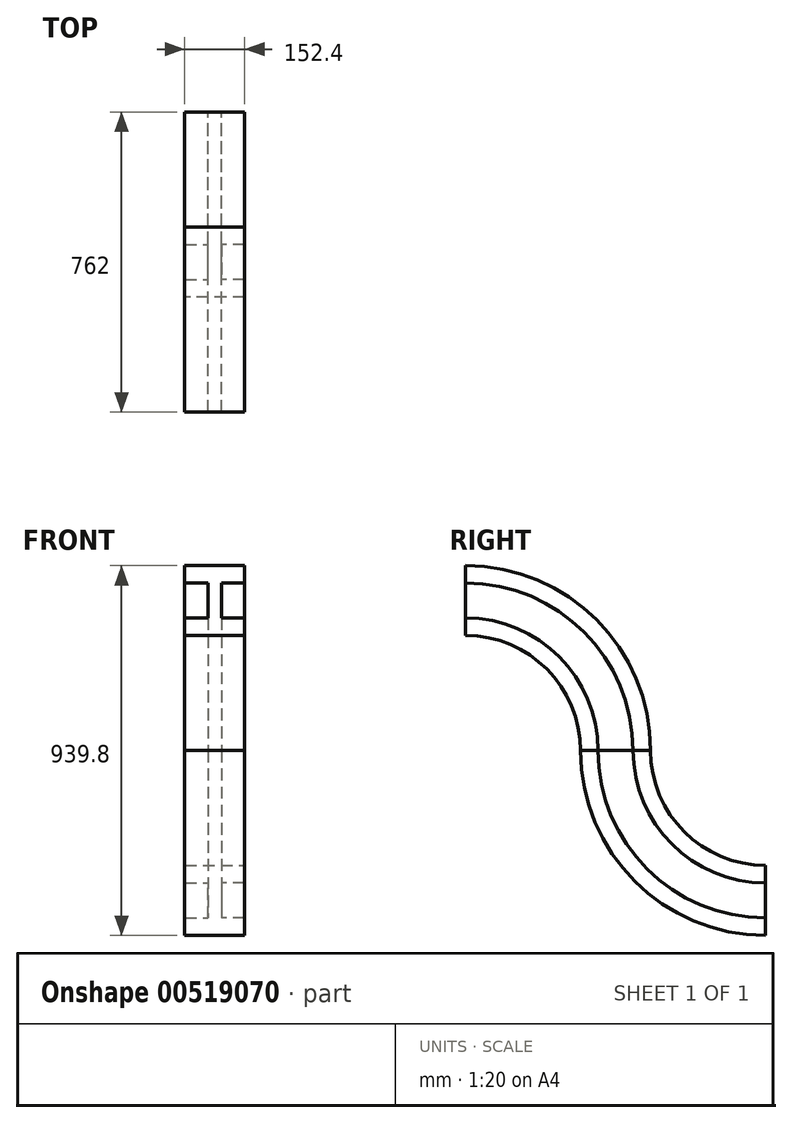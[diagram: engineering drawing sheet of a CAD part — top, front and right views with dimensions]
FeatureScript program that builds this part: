
annotation { "Feature Type Name" : "Feature", "Feature Type Description" : "" }
export const myFeature = defineFeature(function(context is Context, id is Id, definition is map)
    precondition{}
    {
        {
            var Q0;
            Q0=qCreatedBy(makeId("Front.planeOp"),FACE);
            var sketch = newSketch(context, id + "F0", { "sketchPlane" : qUnion([Q0])});
            skLineSegment(sketch, "E0", {"start": v(0, 88.9) * mm, "end": v(76.2, 88.9) * mm});
            skLineSegment(sketch, "E1", {"start": v(76.2, 88.9) * mm, "end": v(76.2, 44.45) * mm});
            skLineSegment(sketch, "E2", {"start": v(76.2, 44.45) * mm, "end": v(17.37, 44.45) * mm});
            skLineSegment(sketch, "E3", {"start": v(0, 88.9) * mm, "end": v(0, -88.9) * mm, "construction": true});
            skLineSegment(sketch, "E4", {"start": v(-17.37, 0) * mm, "end": v(17.37, 0) * mm, "construction": true});
            skLineSegment(sketch, "E5", {"start": v(17.37, 0) * mm, "end": v(17.37, 44.45) * mm});
            skLineSegment(sketch, "E6.MirrorCS", {"start": v(0, 88.9) * mm, "end": v(-76.2, 88.9) * mm});
            skLineSegment(sketch, "E7.MirrorCS", {"start": v(-76.2, 88.9) * mm, "end": v(-76.2, 44.45) * mm});
            skLineSegment(sketch, "E8.MirrorCS", {"start": v(-17.37, 0) * mm, "end": v(-17.37, 44.45) * mm});
            skLineSegment(sketch, "E9.MirrorCS", {"start": v(-76.2, 44.45) * mm, "end": v(-17.37, 44.45) * mm});
            skLineSegment(sketch, "E10.MirrorCS", {"start": v(0, -88.9) * mm, "end": v(-76.2, -88.9) * mm});
            skLineSegment(sketch, "E11.MirrorCS", {"start": v(-76.2, -88.9) * mm, "end": v(-76.2, -44.45) * mm});
            skLineSegment(sketch, "E12.MirrorCS", {"start": v(-76.2, -44.45) * mm, "end": v(-17.37, -44.45) * mm});
            skLineSegment(sketch, "E13.MirrorCS", {"start": v(-17.37, 0) * mm, "end": v(-17.37, -44.45) * mm});
            skLineSegment(sketch, "E14.MirrorCS", {"start": v(76.2, -44.45) * mm, "end": v(17.37, -44.45) * mm});
            skLineSegment(sketch, "E15.MirrorCS", {"start": v(0, -88.9) * mm, "end": v(76.2, -88.9) * mm});
            skLineSegment(sketch, "E16.MirrorCS", {"start": v(17.37, 0) * mm, "end": v(17.37, -44.45) * mm});
            skLineSegment(sketch, "E17.MirrorCS", {"start": v(76.2, -88.9) * mm, "end": v(76.2, -44.45) * mm});
            skSolve(sketch);
        }
        {
            var Q0;
            Q0=qCreatedBy(makeId("Right.planeOp"),FACE);
            var sketch = newSketch(context, id + "F1", { "sketchPlane" : qUnion([Q0])});
            skArc(sketch, "E18", {"start": v(0, 0) * mm, "mid": v(269.4, -111.6) * mm, "end": v(381, -381) * mm});
            skArc(sketch, "E19", {"start": v(381, -381) * mm, "mid": v(492.6, -650.4) * mm, "end": v(762, -762) * mm});
            skSolve(sketch);
        }
        {
            var Q0;
            Q0=makeQuery(id+"F0.imprint","IMPRINT",FACE,{"disambiguationData":[TD([[makeQuery(id+"F0.imprint","IMPRINT",EDGE,{"derivedFrom":sQuery(id+"F0.wireOp",EDGE,"E0")}),-1.0]])]});
            var Q1;
            Q1=sQuery(id+"F1.wireOp",EDGE,"E18");
            sweep(context, id + "F2", {"profiles" : qUnion([Q0]), "path" : qUnion([Q1])});
        }
        {
            var Q0;
            Q0=makeQuery(id+"F0.imprint","IMPRINT",FACE,{"disambiguationData":[TD([[makeQuery(id+"F0.imprint","IMPRINT",EDGE,{"derivedFrom":sQuery(id+"F0.wireOp",EDGE,"E0")}),-1.0]])]});
            var Q1;
            Q1=sQuery(id+"F1.wireOp",EDGE,"E18");
            var Q2;
            Q2=sQuery(id+"F1.wireOp",EDGE,"E19");
            sweep(context, id + "F3", {"profiles" : qUnion([Q0]), "path" : qUnion([Q1, Q2])});
        }
    });
